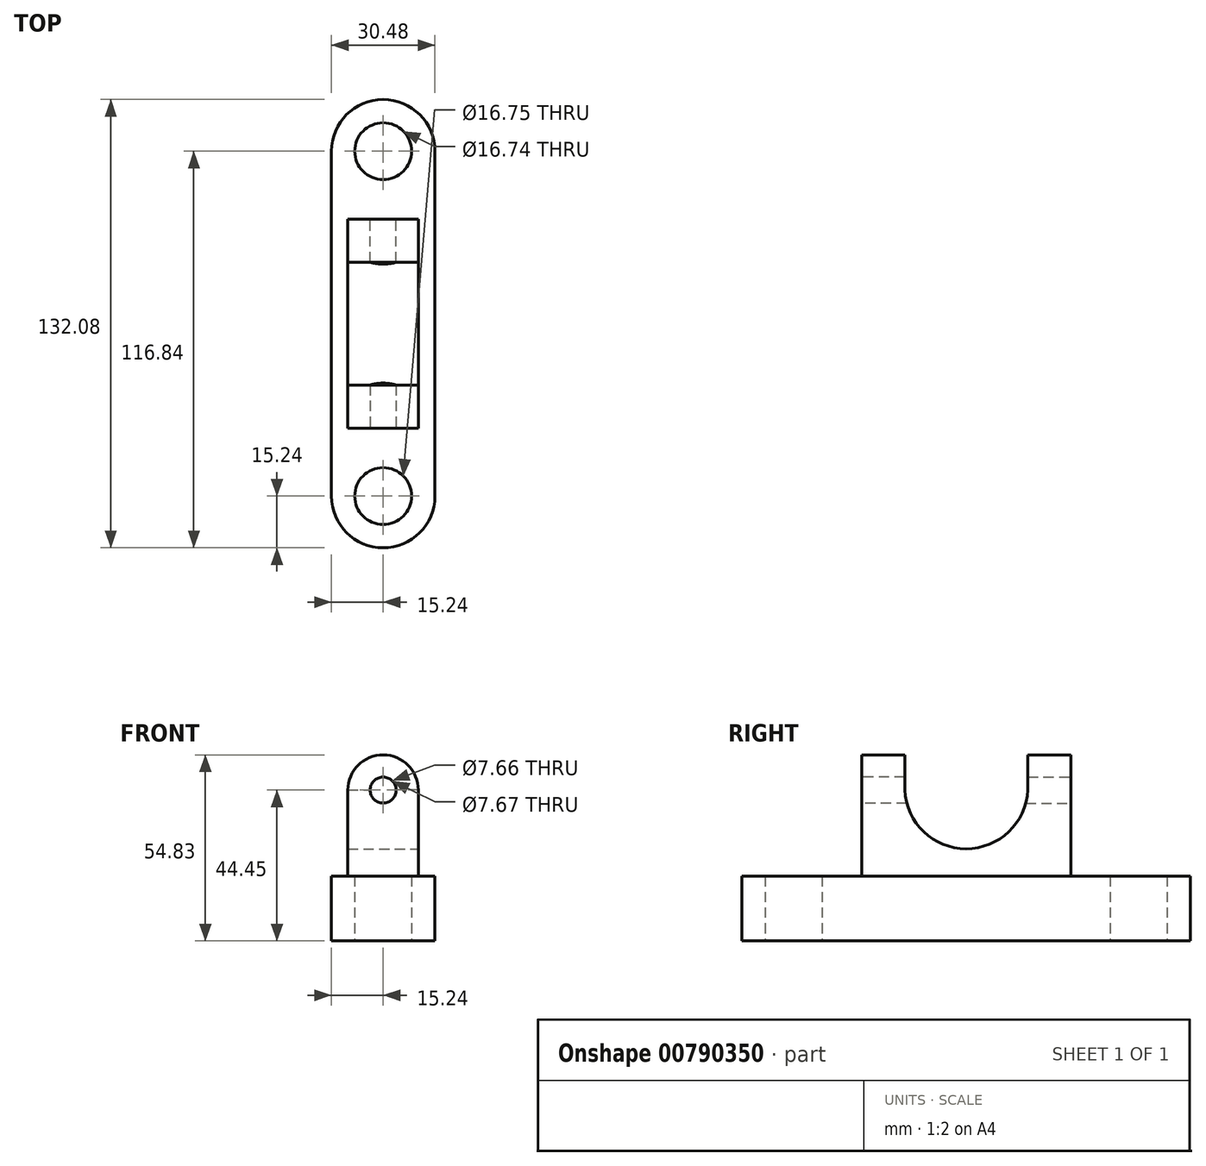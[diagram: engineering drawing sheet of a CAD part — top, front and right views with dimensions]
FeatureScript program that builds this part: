
annotation { "Feature Type Name" : "Feature", "Feature Type Description" : "" }
export const myFeature = defineFeature(function(context is Context, id is Id, definition is map)
    precondition{}
    {
        {
            var Q0;
            Q0=qCreatedBy(makeId("Top.planeOp"),FACE);
            var sketch = newSketch(context, id + "F0", { "sketchPlane" : qUnion([Q0])});
            skLineSegment(sketch, "E0", {"start": v(-15.24, 0) * mm, "end": v(-15.24, -50.8) * mm});
            skLineSegment(sketch, "E1", {"start": v(-15.24, 0) * mm, "end": v(-15.24, 50.8) * mm});
            skLineSegment(sketch, "E2", {"start": v(15.24, 0) * mm, "end": v(15.24, 50.8) * mm});
            skLineSegment(sketch, "E3", {"start": v(15.24, 0) * mm, "end": v(15.24, -50.8) * mm});
            skArc(sketch, "E4", {"start": v(15.24, 50.8) * mm, "mid": v(0, 66.04) * mm, "end": v(-15.24, 50.8) * mm});
            skArc(sketch, "E5", {"start": v(-15.24, -50.8) * mm, "mid": v(0, -66.04) * mm, "end": v(15.24, -50.8) * mm});
            skCircle(sketch, "E6", {"center": v(0, -50.8) * mm, "radius": 8.37 * mm});
            skCircle(sketch, "E7", {"center": v(0, 50.8) * mm, "radius": 8.37 * mm});
            skSolve(sketch);
        }
        {
            var Q0;
            Q0 = qSketchRegion(id + "F0", true);
            extrude(context, id + "F1", {"entities" : qUnion([Q0]), "depth" : 19.05 * mm, "offsetDistance" : 25.4 * mm});
        }
        {
            var Q0;
            Q0=makeQuery(id+"F1.opExtrude","CAP_FACE",FACE,{"disambiguationData":[OSD([sQuery(id+"F0.wireOp",EDGE,"E0"),sQuery(id+"F0.wireOp",EDGE,"E1"),sQuery(id+"F0.wireOp",EDGE,"E2"),sQuery(id+"F0.wireOp",EDGE,"E3"),sQuery(id+"F0.wireOp",EDGE,"E4"),sQuery(id+"F0.wireOp",EDGE,"E5"),sQuery(id+"F0.wireOp",EDGE,"E6"),sQuery(id+"F0.wireOp",EDGE,"E7")])],"isStart":false});
            var sketch = newSketch(context, id + "F2", { "sketchPlane" : qUnion([Q0])});
            skLineSegment(sketch, "E8.bottom", {"start": v(10.38, -30.83) * mm, "end": v(-10.38, -30.83) * mm});
            skLineSegment(sketch, "E8.top", {"start": v(10.38, 30.83) * mm, "end": v(-10.38, 30.83) * mm});
            skLineSegment(sketch, "E8.left", {"start": v(10.38, -30.83) * mm, "end": v(10.38, 30.83) * mm});
            skLineSegment(sketch, "E8.right", {"start": v(-10.38, -30.83) * mm, "end": v(-10.38, 30.83) * mm});
            skPoint(sketch, "E8.middle", {"position": v(0, 0) * mm});
            skSolve(sketch);
        }
        {
            var Q0;
            Q0 = qSketchRegion(id + "F2", true);
            extrude(context, id + "F3", {"entities" : qUnion([Q0]), "operationType" : NewBodyOperationType.ADD, "depth" : 25.4 * mm, "offsetDistance" : 25.4 * mm});
        }
        {
            var Q0;
            Q0=makeQuery(id+"F3.opExtrude","SWEPT_FACE",FACE,{"disambiguationData":[OSD([sQuery(id+"F2.wireOp",EDGE,"E8.left")])]});
            var sketch = newSketch(context, id + "F4", { "sketchPlane" : qUnion([Q0])});
            skLineSegment(sketch, "E9", {"start": v(-30.83, 44.45) * mm, "end": v(-18.13, 44.45) * mm});
            skLineSegment(sketch, "E10", {"start": v(-18.13, 44.45) * mm, "end": v(30.83, 44.45) * mm});
            skLineSegment(sketch, "E11", {"start": v(30.83, 44.45) * mm, "end": v(18.13, 44.45) * mm});
            skArc(sketch, "E12", {"start": v(-18.13, 44.45) * mm, "mid": v(0, 27.16) * mm, "end": v(18.13, 44.45) * mm});
            skSolve(sketch);
        }
        {
            var Q0;
            Q0 = qSketchRegion(id + "F4", true);
            extrude(context, id + "F5", {"entities" : qUnion([Q0]), "operationType" : NewBodyOperationType.REMOVE, "oppositeDirection" : true, "depth" : 25.4 * mm, "offsetDistance" : 25.4 * mm});
        }
        {
            var Q0;
            Q0=makeQuery(id+"F3.opExtrude","SWEPT_FACE",FACE,{"disambiguationData":[OSD([sQuery(id+"F2.wireOp",EDGE,"E8.bottom")])]});
            var sketch = newSketch(context, id + "F6", { "sketchPlane" : qUnion([Q0])});
            skArc(sketch, "E13", {"start": v(10.38, 44.45) * mm, "mid": v(0, 54.83) * mm, "end": v(-10.38, 44.45) * mm});
            skCircle(sketch, "E14", {"center": v(0, 44.45) * mm, "radius": 3.83 * mm});
            skSolve(sketch);
        }
        {
            var Q0;
            Q0=makeQuery(id+"F6.imprint","IMPRINT",FACE,{"disambiguationData":[TD([[makeQuery(id+"F6.imprint","IMPRINT",EDGE,{"derivedFrom":sQuery(id+"F6.wireOp",EDGE,"E13")}),1.0]])]});
            extrude(context, id + "F7", {"entities" : qUnion([Q0]), "operationType" : NewBodyOperationType.ADD, "oppositeDirection" : true, "depth" : 12.7 * mm, "offsetDistance" : 25.4 * mm});
        }
        {
            var Q0;
            Q0 = qSketchRegion(id + "F6", true);
            extrude(context, id + "F8", {"entities" : qUnion([Q0]), "operationType" : NewBodyOperationType.REMOVE, "oppositeDirection" : true, "depth" : 15.24 * mm, "offsetDistance" : 25.4 * mm});
        }
        {
            var Q0;
            Q0=makeQuery(id+"F3.opExtrude","SWEPT_FACE",FACE,{"disambiguationData":[OSD([sQuery(id+"F2.wireOp",EDGE,"E8.top")])]});
            var sketch = newSketch(context, id + "F9", { "sketchPlane" : qUnion([Q0])});
            skArc(sketch, "E15", {"start": v(10.38, 44.45) * mm, "mid": v(0, 54.83) * mm, "end": v(-10.38, 44.45) * mm});
            skCircle(sketch, "E16", {"center": v(0, 44.45) * mm, "radius": 3.84 * mm});
            skSolve(sketch);
        }
        {
            var Q0;
            Q0=makeQuery(id+"F9.imprint","IMPRINT",FACE,{"disambiguationData":[TD([[makeQuery(id+"F9.imprint","IMPRINT",EDGE,{"derivedFrom":sQuery(id+"F9.wireOp",EDGE,"E15")}),1.0]])]});
            extrude(context, id + "F10", {"entities" : qUnion([Q0]), "operationType" : NewBodyOperationType.ADD, "oppositeDirection" : true, "depth" : 12.7 * mm, "offsetDistance" : 25.4 * mm});
        }
        {
            var Q0;
            Q0 = qSketchRegion(id + "F9", true);
            extrude(context, id + "F11", {"entities" : qUnion([Q0]), "operationType" : NewBodyOperationType.REMOVE, "oppositeDirection" : true, "depth" : 15.24 * mm, "offsetDistance" : 25.4 * mm});
        }
    });
